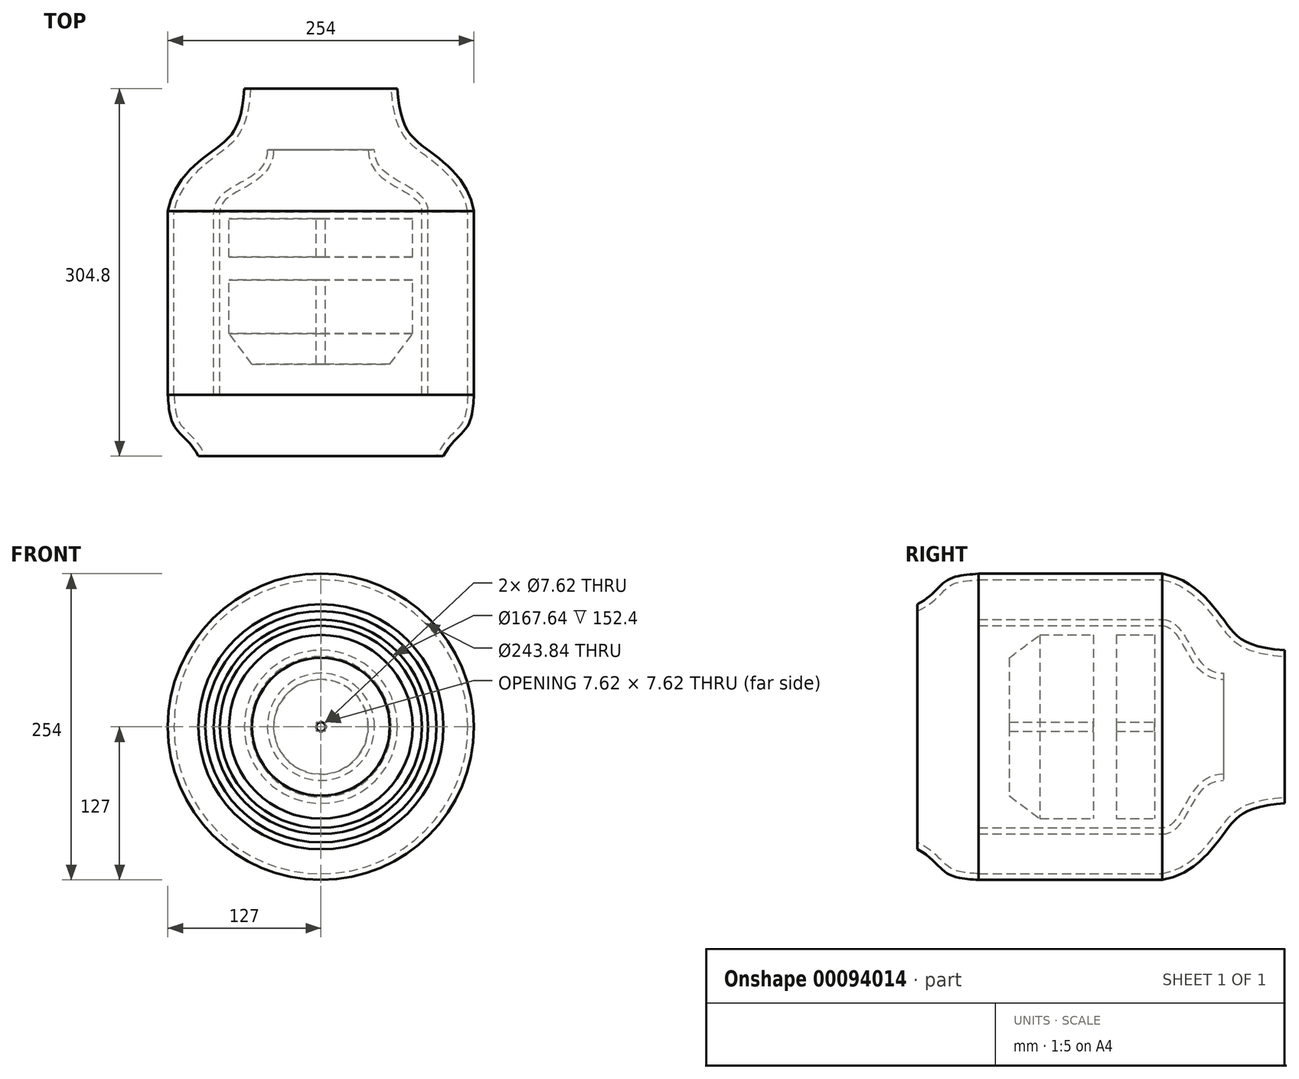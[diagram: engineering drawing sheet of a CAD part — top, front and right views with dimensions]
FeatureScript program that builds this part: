
annotation { "Feature Type Name" : "Feature", "Feature Type Description" : "" }
export const myFeature = defineFeature(function(context is Context, id is Id, definition is map)
    precondition{}
    {
        {
            var Q0;
            Q0=qCreatedBy(makeId("Right.planeOp"),FACE);
            var sketch = newSketch(context, id + "F0", { "sketchPlane" : qUnion([Q0])});
            skLineSegment(sketch, "E0", {"start": v(152.4, 0) * mm, "end": v(-152.4, 0) * mm});
            skPoint(sketch, "E1", {"position": v(0, 0) * mm});
            skLineSegment(sketch, "E2", {"start": v(-152.4, 0) * mm, "end": v(-152.4, 101.6) * mm});
            skLineSegment(sketch, "E3", {"start": v(-152.4, 101.6) * mm, "end": v(-127, 101.6) * mm, "construction": true});
            skLineSegment(sketch, "E4", {"start": v(-127, 101.6) * mm, "end": v(-127, 121.92) * mm, "construction": true});
            skLineSegment(sketch, "E5", {"start": v(-127, 101.6) * mm, "end": v(-101.6, 101.6) * mm, "construction": true});
            skLineSegment(sketch, "E6", {"start": v(-101.6, 101.6) * mm, "end": v(-101.6, 127) * mm, "construction": true});
            skFitSpline(sketch, "E7", {"points": [v(-152.4, 101.6) * mm, v(-127, 121.92) * mm, v(-101.6, 127) * mm], "startDerivative": vector(70.98, 35.75) * mm, "endDerivative": vector(55.23, 4.25) * mm});
            skLineSegment(sketch, "E8", {"start": v(-101.6, 127) * mm, "end": v(50.8, 127) * mm});
            skPoint(sketch, "E9", {"position": v(101.6, 0) * mm});
            skLineSegment(sketch, "E10", {"start": v(101.6, 0) * mm, "end": v(101.6, 88.9) * mm, "construction": true});
            skLineSegment(sketch, "E11", {"start": v(152.4, 0) * mm, "end": v(152.4, 63.5) * mm});
            skFitSpline(sketch, "E12", {"points": [v(50.8, 127) * mm, v(101.6, 88.9) * mm, v(152.4, 63.5) * mm], "startDerivative": vector(144.88, -23.56) * mm, "endDerivative": vector(213.2, -14.75) * mm});
            skLineSegment(sketch, "E13", {"start": v(-101.6, 127) * mm, "end": v(-101.6, 0) * mm, "construction": true});
            skLineSegment(sketch, "E14", {"start": v(-101.6, 0) * mm, "end": v(-101.6, 88.9) * mm});
            skLineSegment(sketch, "E15", {"start": v(-101.6, 88.9) * mm, "end": v(50.8, 88.9) * mm});
            skPoint(sketch, "E16", {"position": v(76.2, 0) * mm});
            skLineSegment(sketch, "E17", {"start": v(101.6, 0) * mm, "end": v(101.6, 44.45) * mm, "construction": true});
            skLineSegment(sketch, "E18", {"start": v(76.2, 0) * mm, "end": v(76.2, 63.5) * mm, "construction": true});
            skFitSpline(sketch, "E19", {"points": [v(50.8, 88.9) * mm, v(76.2, 63.5) * mm, v(101.6, 44.45) * mm], "startDerivative": vector(73.92, 0) * mm, "endDerivative": vector(78.63, 0) * mm});
            skLineSegment(sketch, "E20", {"start": v(101.6, 44.45) * mm, "end": v(76.2, 44.45) * mm, "construction": true});
            skLineSegment(sketch, "E21", {"start": v(50.8, 88.9) * mm, "end": v(76.2, 88.9) * mm, "construction": true});
            skLineSegment(sketch, "E22", {"start": v(101.6, 44.45) * mm, "end": v(101.6, 0) * mm});
            skPoint(sketch, "E23", {"position": v(-76.2, 0) * mm});
            skLineSegment(sketch, "E24", {"start": v(-76.2, 0) * mm, "end": v(-76.2, 57.15) * mm});
            skPoint(sketch, "E25", {"position": v(-50.8, 0) * mm});
            skLineSegment(sketch, "E26", {"start": v(-50.8, 0) * mm, "end": v(-50.8, 76.2) * mm, "construction": true});
            skLineSegment(sketch, "E27", {"start": v(-76.2, 57.15) * mm, "end": v(-50.8, 76.2) * mm});
            skLineSegment(sketch, "E28", {"start": v(-50.8, 76.2) * mm, "end": v(-6.35, 76.2) * mm});
            skLineSegment(sketch, "E29", {"start": v(-6.35, 76.2) * mm, "end": v(-6.35, 0) * mm});
            skLineSegment(sketch, "E30", {"start": v(-6.35, 0) * mm, "end": v(-76.2, 0) * mm});
            skPoint(sketch, "E31", {"position": v(12.7, 0) * mm});
            skLineSegment(sketch, "E32", {"start": v(12.7, 0) * mm, "end": v(12.7, 76.2) * mm});
            skLineSegment(sketch, "E33", {"start": v(12.7, 76.2) * mm, "end": v(44.45, 76.2) * mm});
            skLineSegment(sketch, "E34.bottom", {"start": v(-93.42, 127) * mm, "end": v(-7.63, 127) * mm});
            skLineSegment(sketch, "E35", {"start": v(44.45, 76.2) * mm, "end": v(44.45, 0) * mm});
            skSolve(sketch);
        }
        {
            var Q0;
            {var subQ4=sQuery(id+"F0.wireOp",EDGE,"E2");Q0=makeQuery(id+"F0.imprint","IMPRINT",FACE,{"disambiguationData":[TD([[makeQuery(id+"F0.imprint","IMPRINT",EDGE,{"derivedFrom":subQ4}),-1.0]])]});}
            var Q1;
            {var subQ0=sQuery(id+"F0.wireOp",EDGE,"E14");Q1=makeQuery(id+"F0.imprint","IMPRINT",FACE,{"disambiguationData":[TD([[makeQuery(id+"F0.imprint","IMPRINT",EDGE,{"derivedFrom":subQ0}),-1.0]])]});}
            var Q2;
            {var subQ0=sQuery(id+"F0.wireOp",EDGE,"E32");Q2=makeQuery(id+"F0.imprint","IMPRINT",FACE,{"disambiguationData":[TD([[makeQuery(id+"F0.imprint","IMPRINT",EDGE,{"derivedFrom":subQ0}),-1.0]])]});}
            var Q3;
            Q3=makeQuery(id+"F0.imprint","IMPRINT",FACE,{"disambiguationData":[TD([[makeQuery(id+"F0.imprint","IMPRINT",EDGE,{"derivedFrom":sQuery(id+"F0.wireOp",EDGE,"E24")}),-1.0]])]});
            var Q4;
            Q4=sQuery(id+"F0.wireOp",EDGE,"E0");
            revolve(context, id + "F1", {"entities" : qUnion([Q0, Q1, Q2, Q3]), "axis" : qUnion([Q4]), "revolveType" : RevolveType.SYMMETRIC, "angle" : 360 * degree});
        }
        {
            var Q0;
            Q0=makeQuery(id+"F1.opRevolve","SWEPT_FACE",FACE,{"disambiguationData":[OSD([sQuery(id+"F0.wireOp",EDGE,"E2")])]});
            var Q1;
            Q1=makeQuery(id+"F1.opRevolve","SWEPT_FACE",FACE,{"disambiguationData":[OSD([sQuery(id+"F0.wireOp",EDGE,"E11")])]});
            shell(context, id + "F2", {"entities" : qUnion([Q0, Q1]), "thickness" : 5.08 * mm});
        }
        {
            var Q0;
            Q0=qCreatedBy(makeId("Front.planeOp"),FACE);
            var sketch = newSketch(context, id + "F3", { "sketchPlane" : qUnion([Q0])});
            skCircle(sketch, "E36", {"center": v(0, 0) * mm, "radius": 3.18 * mm});
            skCircle(sketch, "E37", {"center": v(0, 0) * mm, "radius": 3.81 * mm});
            skSolve(sketch);
        }
        {
            var Q0;
            {var subQ0=sQuery(id+"F0.wireOp",EDGE,"E14");Q0=makeQuery(id+"F0.imprint","IMPRINT",FACE,{"disambiguationData":[TD([[makeQuery(id+"F0.imprint","IMPRINT",EDGE,{"derivedFrom":subQ0}),-1.0]])]});}
            var Q1;
            Q1=makeQuery(id+"F0.imprint","IMPRINT",FACE,{"disambiguationData":[TD([[makeQuery(id+"F0.imprint","IMPRINT",EDGE,{"derivedFrom":sQuery(id+"F0.wireOp",EDGE,"E24")}),-1.0]])]});
            var Q2;
            {var subQ0=sQuery(id+"F0.wireOp",EDGE,"E32");Q2=makeQuery(id+"F0.imprint","IMPRINT",FACE,{"disambiguationData":[TD([[makeQuery(id+"F0.imprint","IMPRINT",EDGE,{"derivedFrom":subQ0}),-1.0]])]});}
            var Q3;
            Q3=sQuery(id+"F0.wireOp",EDGE,"E0");
            revolve(context, id + "F4", {"entities" : qUnion([Q0, Q1, Q2]), "axis" : qUnion([Q3]), "revolveType" : RevolveType.FULL});
        }
        {
            var Q0;
            Q0=makeQuery(id+"F4.opRevolve","SWEPT_FACE",FACE,{"disambiguationData":[OSD([sQuery(id+"F0.wireOp",EDGE,"E14")])]});
            var Q1;
            Q1=makeQuery(id+"F4.opRevolve","SWEPT_FACE",FACE,{"disambiguationData":[OSD([sQuery(id+"F0.wireOp",EDGE,"E22")])]});
            shell(context, id + "F5", {"entities" : qUnion([Q0, Q1]), "thickness" : 5.08 * mm});
        }
        {
            var Q0;
            Q0=makeQuery(id+"F0.imprint","IMPRINT",FACE,{"disambiguationData":[TD([[makeQuery(id+"F0.imprint","IMPRINT",EDGE,{"derivedFrom":sQuery(id+"F0.wireOp",EDGE,"E24")}),-1.0]])]});
            var Q1;
            {var subQ0=sQuery(id+"F0.wireOp",EDGE,"E32");Q1=makeQuery(id+"F0.imprint","IMPRINT",FACE,{"disambiguationData":[TD([[makeQuery(id+"F0.imprint","IMPRINT",EDGE,{"derivedFrom":subQ0}),-1.0]])]});}
            var Q2;
            Q2=sQuery(id+"F0.wireOp",EDGE,"E0");
            revolve(context, id + "F6", {"entities" : qUnion([Q0, Q1]), "axis" : qUnion([Q2]), "revolveType" : RevolveType.FULL});
        }
        {
            var Q0;
            Q0=makeQuery(id+"F3.imprint","IMPRINT",FACE,{"disambiguationData":[TD([[makeQuery(id+"F3.imprint","IMPRINT",EDGE,{"derivedFrom":sQuery(id+"F3.wireOp",EDGE,"E36")}),-1.0]])]});
            var Q1;
            Q1=makeQuery(id+"F3.imprint","IMPRINT",FACE,{"disambiguationData":[TD([[makeQuery(id+"F3.imprint","IMPRINT",EDGE,{"derivedFrom":sQuery(id+"F3.wireOp",EDGE,"E36")}),1.0]])]});
            extrude(context, id + "F7", {"entities" : qUnion([Q0, Q1]), "operationType" : NewBodyOperationType.REMOVE, "endBound" : BoundingType.SYMMETRIC, "depth" : 2540 * mm});
        }
        {
            var Q0;
            Q0=qCreatedBy(makeId("Front.planeOp"),FACE);
            cPlane(context, id + "F8", {"entities" : qUnion([Q0]), "cplaneType" : CPlaneType.OFFSET, "offset" : 38.1 * mm, "width" : 152.4 * mm, "height" : 152.4 * mm});
        }
    });
